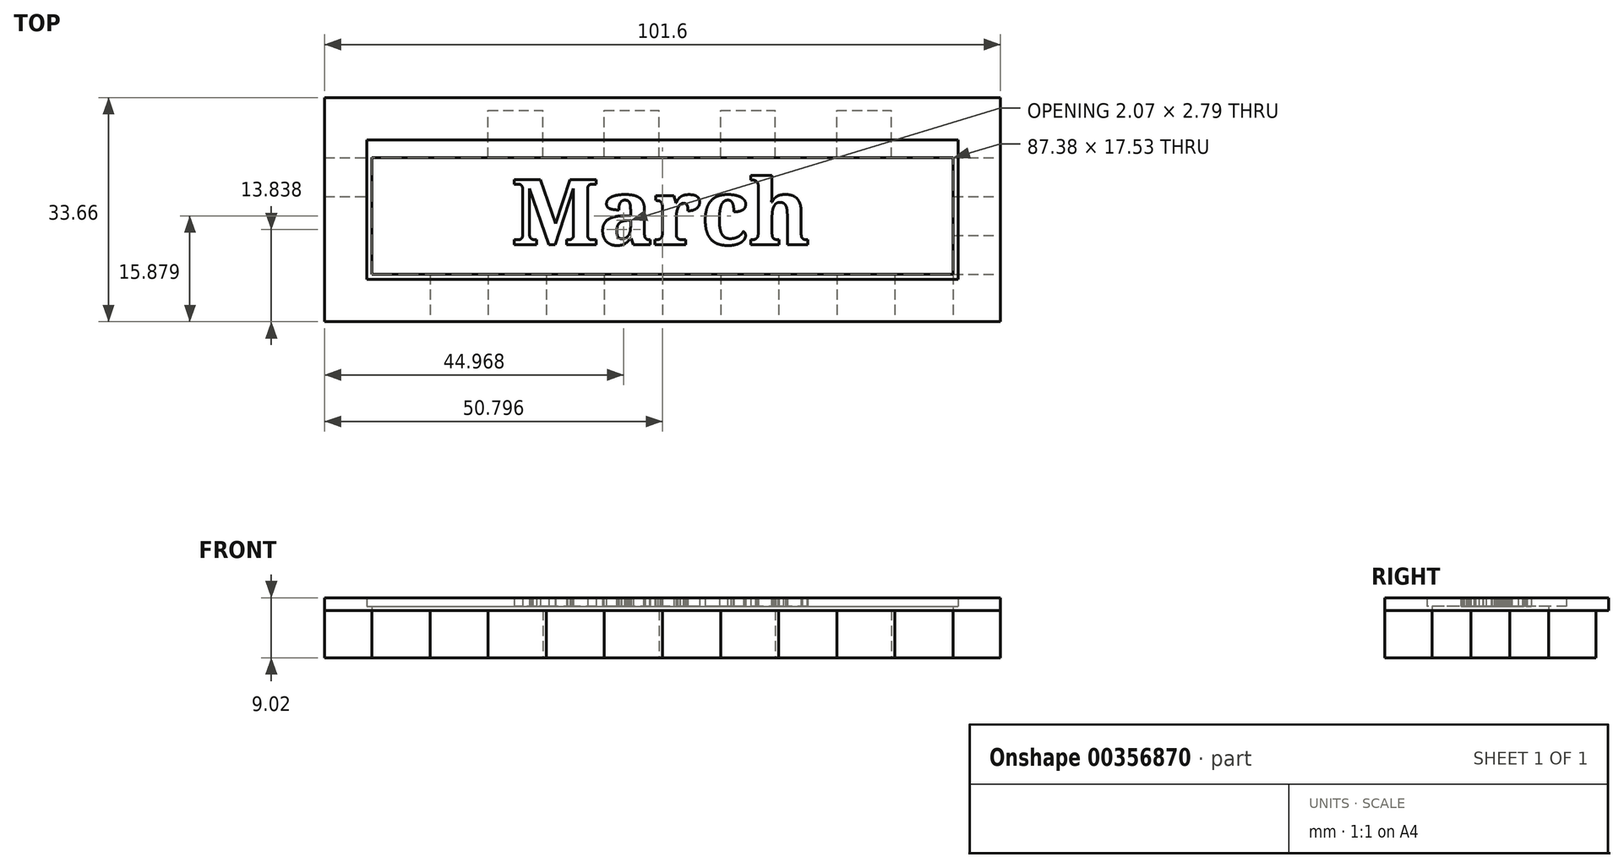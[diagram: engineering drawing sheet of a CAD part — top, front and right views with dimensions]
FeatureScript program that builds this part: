
annotation { "Feature Type Name" : "Feature", "Feature Type Description" : "" }
export const myFeature = defineFeature(function(context is Context, id is Id, definition is map)
    precondition{}
    {
        {
            var Q0;
            Q0=qCreatedBy(makeId("Top.planeOp"),FACE);
            var sketch = newSketch(context, id + "F0", { "sketchPlane" : qUnion([Q0])});
            skLineSegment(sketch, "E0.bottom", {"start": v(-52.12, 11.37) * mm, "end": v(49.48, 11.37) * mm});
            skLineSegment(sketch, "E0.top", {"start": v(-52.12, -20.38) * mm, "end": v(49.48, -20.38) * mm});
            skLineSegment(sketch, "E0.left", {"start": v(-52.12, 11.37) * mm, "end": v(-52.12, -20.38) * mm});
            skLineSegment(sketch, "E0.right", {"start": v(49.48, 11.37) * mm, "end": v(49.48, -20.38) * mm});
            skLineSegment(sketch, "E1.bottom", {"start": v(-52.12, 11.37) * mm, "end": v(-45.01, 11.37) * mm});
            skLineSegment(sketch, "E1.top", {"start": v(-52.12, 4.26) * mm, "end": v(-45.01, 4.26) * mm});
            skLineSegment(sketch, "E1.left", {"start": v(-52.12, 11.37) * mm, "end": v(-52.12, 4.26) * mm});
            skLineSegment(sketch, "E1.right", {"start": v(-45.01, 11.37) * mm, "end": v(-45.01, 4.26) * mm});
            skLineSegment(sketch, "E2.bottom", {"start": v(-45.01, 11.37) * mm, "end": v(-36.78, 11.37) * mm});
            skLineSegment(sketch, "E2.top", {"start": v(-45.01, 4.26) * mm, "end": v(-36.78, 4.26) * mm});
            skLineSegment(sketch, "E2.right", {"start": v(-36.78, 11.37) * mm, "end": v(-36.78, 4.26) * mm});
            skLineSegment(sketch, "E3.bottom", {"start": v(-36.78, 4.26) * mm, "end": v(-27.54, 4.26) * mm});
            skLineSegment(sketch, "E3.top", {"start": v(-36.78, 11.37) * mm, "end": v(-27.54, 11.37) * mm});
            skLineSegment(sketch, "E3.left", {"start": v(-36.78, 4.26) * mm, "end": v(-36.78, 11.37) * mm});
            skLineSegment(sketch, "E3.right", {"start": v(-27.54, 4.26) * mm, "end": v(-27.54, 11.37) * mm});
            skLineSegment(sketch, "E4.bottom", {"start": v(-27.54, 4.26) * mm, "end": v(-19.3, 4.26) * mm});
            skLineSegment(sketch, "E4.top", {"start": v(-27.54, 11.37) * mm, "end": v(-19.3, 11.37) * mm});
            skLineSegment(sketch, "E4.right", {"start": v(-19.3, 4.26) * mm, "end": v(-19.3, 11.37) * mm});
            skLineSegment(sketch, "E5.bottom", {"start": v(-19.3, 4.26) * mm, "end": v(-10.06, 4.26) * mm});
            skLineSegment(sketch, "E5.top", {"start": v(-19.3, 11.37) * mm, "end": v(-10.06, 11.37) * mm});
            skLineSegment(sketch, "E5.right", {"start": v(-10.06, 4.26) * mm, "end": v(-10.06, 11.37) * mm});
            skLineSegment(sketch, "E6.bottom", {"start": v(-10.06, 4.26) * mm, "end": v(-10.06, 4.26) * mm});
            skLineSegment(sketch, "E6.top", {"start": v(-10.06, 11.37) * mm, "end": v(-10.06, 11.37) * mm});
            skLineSegment(sketch, "E7.bottom", {"start": v(-10.06, 4.26) * mm, "end": v(-1.83, 4.26) * mm});
            skLineSegment(sketch, "E7.top", {"start": v(-10.06, 11.37) * mm, "end": v(-1.83, 11.37) * mm});
            skLineSegment(sketch, "E7.right", {"start": v(-1.83, 4.26) * mm, "end": v(-1.83, 11.37) * mm});
            skLineSegment(sketch, "E8.bottom", {"start": v(-1.83, 4.26) * mm, "end": v(7.41, 4.26) * mm});
            skLineSegment(sketch, "E8.top", {"start": v(-1.83, 11.37) * mm, "end": v(7.41, 11.37) * mm});
            skLineSegment(sketch, "E8.right", {"start": v(7.41, 4.26) * mm, "end": v(7.41, 11.37) * mm});
            skLineSegment(sketch, "E9.bottom", {"start": v(7.41, 4.26) * mm, "end": v(15.64, 4.26) * mm});
            skLineSegment(sketch, "E9.top", {"start": v(7.41, 11.37) * mm, "end": v(15.64, 11.37) * mm});
            skLineSegment(sketch, "E9.right", {"start": v(15.64, 4.26) * mm, "end": v(15.64, 11.37) * mm});
            skLineSegment(sketch, "E10.bottom", {"start": v(15.64, 4.26) * mm, "end": v(24.89, 4.26) * mm});
            skLineSegment(sketch, "E10.top", {"start": v(15.64, 11.37) * mm, "end": v(24.89, 11.37) * mm});
            skLineSegment(sketch, "E10.right", {"start": v(24.89, 4.26) * mm, "end": v(24.89, 11.37) * mm});
            skLineSegment(sketch, "E11.bottom", {"start": v(24.89, 4.26) * mm, "end": v(24.89, 4.26) * mm});
            skLineSegment(sketch, "E11.top", {"start": v(24.89, 11.37) * mm, "end": v(24.89, 11.37) * mm});
            skLineSegment(sketch, "E12.bottom", {"start": v(24.89, 4.26) * mm, "end": v(33.12, 4.26) * mm});
            skLineSegment(sketch, "E12.top", {"start": v(24.89, 11.37) * mm, "end": v(33.12, 11.37) * mm});
            skLineSegment(sketch, "E12.right", {"start": v(33.12, 4.26) * mm, "end": v(33.12, 11.37) * mm});
            skLineSegment(sketch, "E13.bottom", {"start": v(33.12, 4.26) * mm, "end": v(42.36, 4.26) * mm});
            skLineSegment(sketch, "E13.top", {"start": v(33.12, 11.37) * mm, "end": v(42.36, 11.37) * mm});
            skLineSegment(sketch, "E13.right", {"start": v(42.36, 4.26) * mm, "end": v(42.36, 11.37) * mm});
            skLineSegment(sketch, "E14.bottom", {"start": v(42.36, 4.26) * mm, "end": v(49.48, 4.26) * mm});
            skLineSegment(sketch, "E14.top", {"start": v(42.36, 11.37) * mm, "end": v(49.48, 11.37) * mm});
            skLineSegment(sketch, "E14.right", {"start": v(49.48, 4.26) * mm, "end": v(49.48, 11.37) * mm});
            skLineSegment(sketch, "E15.bottom", {"start": v(-52.12, -20.38) * mm, "end": v(-45.01, -20.38) * mm});
            skLineSegment(sketch, "E15.top", {"start": v(-52.12, -13.26) * mm, "end": v(-45.01, -13.26) * mm});
            skLineSegment(sketch, "E15.left", {"start": v(-52.12, -20.38) * mm, "end": v(-52.12, -13.26) * mm});
            skLineSegment(sketch, "E15.right", {"start": v(-45.01, -20.38) * mm, "end": v(-45.01, -13.26) * mm});
            skLineSegment(sketch, "E16.bottom", {"start": v(-45.01, -13.26) * mm, "end": v(-45.01, -13.26) * mm});
            skLineSegment(sketch, "E16.top", {"start": v(-45.01, -20.38) * mm, "end": v(-45.01, -20.38) * mm});
            skLineSegment(sketch, "E16.left", {"start": v(-45.01, -13.26) * mm, "end": v(-45.01, -20.38) * mm});
            skLineSegment(sketch, "E16.right", {"start": v(-45.01, -13.26) * mm, "end": v(-45.01, -20.38) * mm});
            skLineSegment(sketch, "E17.bottom", {"start": v(-45.01, -13.26) * mm, "end": v(-36.27, -13.26) * mm});
            skLineSegment(sketch, "E17.top", {"start": v(-45.01, -20.38) * mm, "end": v(-36.27, -20.38) * mm});
            skLineSegment(sketch, "E17.right", {"start": v(-36.27, -13.26) * mm, "end": v(-36.27, -20.38) * mm});
            skLineSegment(sketch, "E18.bottom", {"start": v(-36.27, -13.26) * mm, "end": v(-36.27, -13.26) * mm});
            skLineSegment(sketch, "E18.top", {"start": v(-36.27, -20.38) * mm, "end": v(-36.27, -20.38) * mm});
            skLineSegment(sketch, "E19.bottom", {"start": v(-36.27, -13.26) * mm, "end": v(-27.54, -13.26) * mm});
            skLineSegment(sketch, "E19.top", {"start": v(-36.27, -20.38) * mm, "end": v(-27.54, -20.38) * mm});
            skLineSegment(sketch, "E19.right", {"start": v(-27.54, -13.26) * mm, "end": v(-27.54, -20.38) * mm});
            skLineSegment(sketch, "E20.bottom", {"start": v(-27.54, -13.26) * mm, "end": v(-18.8, -13.26) * mm});
            skLineSegment(sketch, "E20.top", {"start": v(-27.54, -20.38) * mm, "end": v(-18.8, -20.38) * mm});
            skLineSegment(sketch, "E20.right", {"start": v(-18.8, -13.26) * mm, "end": v(-18.8, -20.38) * mm});
            skLineSegment(sketch, "E21.bottom", {"start": v(-18.8, -13.26) * mm, "end": v(-10.06, -13.26) * mm});
            skLineSegment(sketch, "E21.top", {"start": v(-18.8, -20.38) * mm, "end": v(-10.06, -20.38) * mm});
            skLineSegment(sketch, "E21.right", {"start": v(-10.06, -13.26) * mm, "end": v(-10.06, -20.38) * mm});
            skLineSegment(sketch, "E22.bottom", {"start": v(-10.06, -13.26) * mm, "end": v(-1.32, -13.26) * mm});
            skLineSegment(sketch, "E22.top", {"start": v(-10.06, -20.38) * mm, "end": v(-1.32, -20.38) * mm});
            skLineSegment(sketch, "E22.right", {"start": v(-1.32, -13.26) * mm, "end": v(-1.32, -20.38) * mm});
            skLineSegment(sketch, "E23.bottom", {"start": v(-1.32, -13.26) * mm, "end": v(7.41, -13.26) * mm});
            skLineSegment(sketch, "E23.top", {"start": v(-1.32, -20.38) * mm, "end": v(7.41, -20.38) * mm});
            skLineSegment(sketch, "E23.right", {"start": v(7.41, -13.26) * mm, "end": v(7.41, -20.38) * mm});
            skLineSegment(sketch, "E24.bottom", {"start": v(7.41, -13.26) * mm, "end": v(16.15, -13.26) * mm});
            skLineSegment(sketch, "E24.top", {"start": v(7.41, -20.38) * mm, "end": v(16.15, -20.38) * mm});
            skLineSegment(sketch, "E24.right", {"start": v(16.15, -13.26) * mm, "end": v(16.15, -20.38) * mm});
            skLineSegment(sketch, "E25.bottom", {"start": v(16.15, -13.26) * mm, "end": v(24.89, -13.26) * mm});
            skLineSegment(sketch, "E25.top", {"start": v(16.15, -20.38) * mm, "end": v(24.89, -20.38) * mm});
            skLineSegment(sketch, "E25.right", {"start": v(24.89, -13.26) * mm, "end": v(24.89, -20.38) * mm});
            skLineSegment(sketch, "E26.bottom", {"start": v(24.89, -13.26) * mm, "end": v(33.63, -13.26) * mm});
            skLineSegment(sketch, "E26.top", {"start": v(24.89, -20.38) * mm, "end": v(33.63, -20.38) * mm});
            skLineSegment(sketch, "E26.right", {"start": v(33.63, -13.26) * mm, "end": v(33.63, -20.38) * mm});
            skLineSegment(sketch, "E27.bottom", {"start": v(33.63, -13.26) * mm, "end": v(42.36, -13.26) * mm});
            skLineSegment(sketch, "E27.top", {"start": v(33.63, -20.38) * mm, "end": v(42.36, -20.38) * mm});
            skLineSegment(sketch, "E27.right", {"start": v(42.36, -13.26) * mm, "end": v(42.36, -20.38) * mm});
            skLineSegment(sketch, "E28.bottom", {"start": v(42.36, -13.26) * mm, "end": v(49.48, -13.26) * mm});
            skLineSegment(sketch, "E28.top", {"start": v(42.36, -20.38) * mm, "end": v(49.48, -20.38) * mm});
            skLineSegment(sketch, "E28.right", {"start": v(49.48, -13.26) * mm, "end": v(49.48, -20.38) * mm});
            skLineSegment(sketch, "E29.top", {"start": v(-52.12, -1.58) * mm, "end": v(-45.01, -1.58) * mm});
            skLineSegment(sketch, "E29.left", {"start": v(-52.12, 4.26) * mm, "end": v(-52.12, -1.58) * mm});
            skLineSegment(sketch, "E29.right", {"start": v(-45.01, 4.26) * mm, "end": v(-45.01, -1.58) * mm});
            skLineSegment(sketch, "E30.top", {"start": v(-52.12, -7.42) * mm, "end": v(-45.01, -7.42) * mm});
            skLineSegment(sketch, "E30.left", {"start": v(-52.12, -1.58) * mm, "end": v(-52.12, -7.42) * mm});
            skLineSegment(sketch, "E30.right", {"start": v(-45.01, -1.58) * mm, "end": v(-45.01, -7.42) * mm});
            skLineSegment(sketch, "E31.bottom", {"start": v(-45.01, -7.42) * mm, "end": v(-52.12, -7.42) * mm});
            skLineSegment(sketch, "E31.top", {"start": v(-45.01, -13.26) * mm, "end": v(-52.12, -13.26) * mm});
            skLineSegment(sketch, "E31.left", {"start": v(-45.01, -7.42) * mm, "end": v(-45.01, -13.26) * mm});
            skLineSegment(sketch, "E31.right", {"start": v(-52.12, -7.42) * mm, "end": v(-52.12, -13.26) * mm});
            skLineSegment(sketch, "E32.top", {"start": v(42.36, -1.58) * mm, "end": v(49.48, -1.58) * mm});
            skLineSegment(sketch, "E32.left", {"start": v(42.36, 4.26) * mm, "end": v(42.36, -1.58) * mm});
            skLineSegment(sketch, "E32.right", {"start": v(49.48, 4.26) * mm, "end": v(49.48, -1.58) * mm});
            skLineSegment(sketch, "E33.top", {"start": v(42.36, -7.42) * mm, "end": v(49.48, -7.42) * mm});
            skLineSegment(sketch, "E33.left", {"start": v(42.36, -1.58) * mm, "end": v(42.36, -7.42) * mm});
            skLineSegment(sketch, "E33.right", {"start": v(49.48, -1.58) * mm, "end": v(49.48, -7.42) * mm});
            skLineSegment(sketch, "E34.left", {"start": v(42.36, -7.42) * mm, "end": v(42.36, -13.26) * mm});
            skLineSegment(sketch, "E34.right", {"start": v(49.48, -7.42) * mm, "end": v(49.48, -13.26) * mm});
            skSolve(sketch);
        }
        {
            var Q0;
            Q0=makeQuery(id+"F0.imprint","IMPRINT",FACE,{"disambiguationData":[TD([[makeQuery(id+"F0.imprint","IMPRINT",EDGE,{"derivedFrom":sQuery(id+"F0.wireOp",EDGE,"E2.top")}),-1.0]])]});
            var Q1;
            Q1=makeQuery(id+"F0.imprint","IMPRINT",FACE,{"disambiguationData":[TD([[makeQuery(id+"F0.imprint","IMPRINT",EDGE,{"derivedFrom":sQuery(id+"F0.wireOp",EDGE,"E2.bottom")}),-1.0]])]});
            var Q2;
            Q2=makeQuery(id+"F0.imprint","IMPRINT",FACE,{"disambiguationData":[TD([[makeQuery(id+"F0.imprint","IMPRINT",EDGE,{"derivedFrom":sQuery(id+"F0.wireOp",EDGE,"E4.bottom")}),1.0]])]});
            var Q3;
            Q3=makeQuery(id+"F0.imprint","IMPRINT",FACE,{"disambiguationData":[TD([[makeQuery(id+"F0.imprint","IMPRINT",EDGE,{"derivedFrom":sQuery(id+"F0.wireOp",EDGE,"E7.bottom")}),1.0]])]});
            var Q4;
            Q4=makeQuery(id+"F0.imprint","IMPRINT",FACE,{"disambiguationData":[TD([[makeQuery(id+"F0.imprint","IMPRINT",EDGE,{"derivedFrom":sQuery(id+"F0.wireOp",EDGE,"E9.bottom")}),1.0]])]});
            var Q5;
            Q5=makeQuery(id+"F0.imprint","IMPRINT",FACE,{"disambiguationData":[TD([[makeQuery(id+"F0.imprint","IMPRINT",EDGE,{"derivedFrom":sQuery(id+"F0.wireOp",EDGE,"E12.bottom")}),1.0]])]});
            var Q6;
            Q6=makeQuery(id+"F0.imprint","IMPRINT",FACE,{"disambiguationData":[TD([[makeQuery(id+"F0.imprint","IMPRINT",EDGE,{"derivedFrom":sQuery(id+"F0.wireOp",EDGE,"E14.bottom")}),-1.0]])]});
            var Q7;
            Q7=makeQuery(id+"F0.imprint","IMPRINT",FACE,{"disambiguationData":[TD([[makeQuery(id+"F0.imprint","IMPRINT",EDGE,{"derivedFrom":sQuery(id+"F0.wireOp",EDGE,"E33.top")}),-1.0]])]});
            var Q8;
            Q8=makeQuery(id+"F0.imprint","IMPRINT",FACE,{"disambiguationData":[TD([[makeQuery(id+"F0.imprint","IMPRINT",EDGE,{"derivedFrom":sQuery(id+"F0.wireOp",EDGE,"E27.bottom")}),-1.0]])]});
            var Q9;
            Q9=makeQuery(id+"F0.imprint","IMPRINT",FACE,{"disambiguationData":[TD([[makeQuery(id+"F0.imprint","IMPRINT",EDGE,{"derivedFrom":sQuery(id+"F0.wireOp",EDGE,"E25.bottom")}),-1.0]])]});
            var Q10;
            Q10=makeQuery(id+"F0.imprint","IMPRINT",FACE,{"disambiguationData":[TD([[makeQuery(id+"F0.imprint","IMPRINT",EDGE,{"derivedFrom":sQuery(id+"F0.wireOp",EDGE,"E23.bottom")}),-1.0]])]});
            var Q11;
            Q11=makeQuery(id+"F0.imprint","IMPRINT",FACE,{"disambiguationData":[TD([[makeQuery(id+"F0.imprint","IMPRINT",EDGE,{"derivedFrom":sQuery(id+"F0.wireOp",EDGE,"E21.bottom")}),-1.0]])]});
            var Q12;
            Q12=makeQuery(id+"F0.imprint","IMPRINT",FACE,{"disambiguationData":[TD([[makeQuery(id+"F0.imprint","IMPRINT",EDGE,{"derivedFrom":sQuery(id+"F0.wireOp",EDGE,"E19.bottom")}),-1.0]])]});
            var Q13;
            Q13=makeQuery(id+"F0.imprint","IMPRINT",FACE,{"disambiguationData":[TD([[makeQuery(id+"F0.imprint","IMPRINT",EDGE,{"derivedFrom":sQuery(id+"F0.wireOp",EDGE,"E31.bottom")}),1.0]])]});
            var Q14;
            Q14=makeQuery(id+"F0.imprint","IMPRINT",FACE,{"disambiguationData":[TD([[makeQuery(id+"F0.imprint","IMPRINT",EDGE,{"derivedFrom":sQuery(id+"F0.wireOp",EDGE,"E1.top")}),-1.0]])]});
            extrude(context, id + "F1", {"entities" : qUnion([Q0, Q1, Q2, Q3, Q4, Q5, Q6, Q7, Q8, Q9, Q10, Q11, Q12, Q13, Q14]), "depth" : 7.11 * mm});
        }
        {
            var Q0;
            Q0=makeQuery(id+"F1.opExtrude","CAP_FACE",FACE,{"disambiguationData":[OSD([sQuery(id+"F0.wireOp",EDGE,"E2.bottom"),sQuery(id+"F0.wireOp",EDGE,"E1.right"),sQuery(id+"F0.wireOp",EDGE,"E3.bottom"),sQuery(id+"F0.wireOp",EDGE,"E3.left"),sQuery(id+"F0.wireOp",EDGE,"E4.top"),sQuery(id+"F0.wireOp",EDGE,"E3.right"),sQuery(id+"F0.wireOp",EDGE,"E5.bottom"),sQuery(id+"F0.wireOp",EDGE,"E4.right"),sQuery(id+"F0.wireOp",EDGE,"E6.top"),sQuery(id+"F0.wireOp",EDGE,"E5.right"),sQuery(id+"F0.wireOp",EDGE,"E7.bottom"),sQuery(id+"F0.wireOp",EDGE,"E5.right"),sQuery(id+"F0.wireOp",EDGE,"E8.top"),sQuery(id+"F0.wireOp",EDGE,"E7.right"),sQuery(id+"F0.wireOp",EDGE,"E9.bottom"),sQuery(id+"F0.wireOp",EDGE,"E8.right"),sQuery(id+"F0.wireOp",EDGE,"E10.top"),sQuery(id+"F0.wireOp",EDGE,"E9.right"),sQuery(id+"F0.wireOp",EDGE,"E11.bottom"),sQuery(id+"F0.wireOp",EDGE,"E10.right"),sQuery(id+"F0.wireOp",EDGE,"E12.top"),sQuery(id+"F0.wireOp",EDGE,"E10.right"),sQuery(id+"F0.wireOp",EDGE,"E13.bottom"),sQuery(id+"F0.wireOp",EDGE,"E12.right"),sQuery(id+"F0.wireOp",EDGE,"E16.bottom"),sQuery(id+"F0.wireOp",EDGE,"E17.top"),sQuery(id+"F0.wireOp",EDGE,"E16.left"),sQuery(id+"F0.wireOp",EDGE,"E18.bottom"),sQuery(id+"F0.wireOp",EDGE,"E17.right"),sQuery(id+"F0.wireOp",EDGE,"E19.top"),sQuery(id+"F0.wireOp",EDGE,"E17.right"),sQuery(id+"F0.wireOp",EDGE,"E20.bottom"),sQuery(id+"F0.wireOp",EDGE,"E19.right"),sQuery(id+"F0.wireOp",EDGE,"E21.top"),sQuery(id+"F0.wireOp",EDGE,"E20.right"),sQuery(id+"F0.wireOp",EDGE,"E22.bottom"),sQuery(id+"F0.wireOp",EDGE,"E21.right"),sQuery(id+"F0.wireOp",EDGE,"E23.top"),sQuery(id+"F0.wireOp",EDGE,"E22.right"),sQuery(id+"F0.wireOp",EDGE,"E24.bottom"),sQuery(id+"F0.wireOp",EDGE,"E23.right"),sQuery(id+"F0.wireOp",EDGE,"E25.top"),sQuery(id+"F0.wireOp",EDGE,"E24.right"),sQuery(id+"F0.wireOp",EDGE,"E26.bottom"),sQuery(id+"F0.wireOp",EDGE,"E25.right"),sQuery(id+"F0.wireOp",EDGE,"E27.top"),sQuery(id+"F0.wireOp",EDGE,"E26.right"),sQuery(id+"F0.wireOp",EDGE,"E27.right"),sQuery(id+"F0.wireOp",EDGE,"E1.top"),sQuery(id+"F0.wireOp",EDGE,"E29.left"),sQuery(id+"F0.wireOp",EDGE,"E29.top"),sQuery(id+"F0.wireOp",EDGE,"E30.right"),sQuery(id+"F0.wireOp",EDGE,"E31.bottom"),sQuery(id+"F0.wireOp",EDGE,"E31.top"),sQuery(id+"F0.wireOp",EDGE,"E31.right"),sQuery(id+"F0.wireOp",EDGE,"E14.bottom"),sQuery(id+"F0.wireOp",EDGE,"E32.right"),sQuery(id+"F0.wireOp",EDGE,"E32.top"),sQuery(id+"F0.wireOp",EDGE,"E33.left"),sQuery(id+"F0.wireOp",EDGE,"E33.top"),sQuery(id+"F0.wireOp",EDGE,"E28.bottom"),sQuery(id+"F0.wireOp",EDGE,"E34.right")])],"isStart":false});
            var sketch = newSketch(context, id + "F2", { "sketchPlane" : qUnion([Q0])});
            skLineSegment(sketch, "E35.bottom", {"start": v(-52.12, -20.38) * mm, "end": v(-45.01, -20.38) * mm});
            skLineSegment(sketch, "E35.top", {"start": v(-52.12, 13.28) * mm, "end": v(-45.01, 13.28) * mm});
            skLineSegment(sketch, "E35.left", {"start": v(-52.12, -20.38) * mm, "end": v(-52.12, 13.28) * mm});
            skLineSegment(sketch, "E35.right", {"start": v(-45.01, -20.38) * mm, "end": v(-45.01, 13.28) * mm});
            skLineSegment(sketch, "E36.bottom", {"start": v(-52.12, -20.38) * mm, "end": v(49.48, -20.38) * mm});
            skLineSegment(sketch, "E36.top", {"start": v(-52.12, -13.26) * mm, "end": v(49.48, -13.26) * mm});
            skLineSegment(sketch, "E36.left", {"start": v(-52.12, -20.38) * mm, "end": v(-52.12, -13.26) * mm});
            skLineSegment(sketch, "E36.right", {"start": v(49.48, -20.38) * mm, "end": v(49.48, -13.26) * mm});
            skPoint(sketch, "E37.oppositeSnap0", {"position": v(42.36, -4.5) * mm});
            skLineSegment(sketch, "E37.bottom", {"start": v(49.48, -20.38) * mm, "end": v(42.36, -20.38) * mm});
            skLineSegment(sketch, "E37.top", {"start": v(49.48, 13.28) * mm, "end": v(42.36, 13.28) * mm});
            skLineSegment(sketch, "E37.left", {"start": v(49.48, -20.38) * mm, "end": v(49.48, 13.28) * mm});
            skLineSegment(sketch, "E37.right", {"start": v(42.36, -20.38) * mm, "end": v(42.36, 13.28) * mm});
            skLineSegment(sketch, "E38.bottom", {"start": v(-52.12, 13.28) * mm, "end": v(49.48, 13.28) * mm});
            skLineSegment(sketch, "E38.top", {"start": v(-52.12, 4.26) * mm, "end": v(49.48, 4.26) * mm});
            skLineSegment(sketch, "E38.left", {"start": v(-52.12, 13.28) * mm, "end": v(-52.12, 4.26) * mm});
            skLineSegment(sketch, "E38.right", {"start": v(49.48, 13.28) * mm, "end": v(49.48, 4.26) * mm});
            skSolve(sketch);
        }
        {
            var Q0;
            Q0=qSketchRegion(id+"F2",true);
            var Q1;
            {var subQ5=sQuery(id+"F2.wireOp",EDGE,"E36.top");var subQ10=sQuery(id+"F2.wireOp",EDGE,"E35.right");var subQ12=makeQuery(id+"F2.imprint","INTERSECT",VERTEX,{"derivedFrom":[makeQuery(id+"F1.opExtrude","CAP_EDGE",EDGE,{"disambiguationData":[OSD([sQuery(id+"F0.wireOp",EDGE,"E31.bottom")])],"isStart":false}),subQ10]});var subQ24=makeQuery(id+"F2.imprint","INTERSECT",VERTEX,{"derivedFrom":[subQ10,subQ5]});Q1=makeQuery(id+"F2.imprint","IMPRINT",FACE,{"disambiguationData":[TD([[makeQuery(id+"F2.imprint","IMPRINT",EDGE,{"disambiguationData":[TD([[subQ12,1.0],[subQ24,-1.0]])],"derivedFrom":subQ10}),-1.0]])]});}
            extrude(context, id + "F3", {"entities" : qUnion([Q0, Q1]), "depth" : 0.64 * mm});
        }
        {
            var Q0;
            Q0=makeQuery(id+"F3.opExtrude","CAP_FACE",FACE,{"disambiguationData":[OSD([sQuery(id+"F2.wireOp",EDGE,"E35.left"),sQuery(id+"F2.wireOp",EDGE,"E36.bottom"),sQuery(id+"F2.wireOp",EDGE,"E36.left"),sQuery(id+"F2.wireOp",EDGE,"E37.bottom"),sQuery(id+"F2.wireOp",EDGE,"E37.left"),sQuery(id+"F2.wireOp",EDGE,"E38.bottom"),sQuery(id+"F2.wireOp",EDGE,"E38.left"),sQuery(id+"F2.wireOp",EDGE,"E38.right")])],"isStart":false});
            var sketch = newSketch(context, id + "F4", { "sketchPlane" : qUnion([Q0])});
            skLineSegment(sketch, "E39.bottom", {"start": v(-52.12, 13.28) * mm, "end": v(49.48, 13.28) * mm});
            skLineSegment(sketch, "E39.top", {"start": v(-52.12, 6.93) * mm, "end": v(49.48, 6.93) * mm});
            skLineSegment(sketch, "E39.left", {"start": v(-52.12, 13.28) * mm, "end": v(-52.12, 6.93) * mm});
            skLineSegment(sketch, "E39.right", {"start": v(49.48, 13.28) * mm, "end": v(49.48, 6.93) * mm});
            skLineSegment(sketch, "E40.bottom", {"start": v(-52.12, 13.28) * mm, "end": v(-45.77, 13.28) * mm});
            skLineSegment(sketch, "E40.top", {"start": v(-52.12, -20.38) * mm, "end": v(-45.77, -20.38) * mm});
            skLineSegment(sketch, "E40.left", {"start": v(-52.12, 13.28) * mm, "end": v(-52.12, -20.38) * mm});
            skLineSegment(sketch, "E40.right", {"start": v(-45.77, 13.28) * mm, "end": v(-45.77, -20.38) * mm});
            skLineSegment(sketch, "E41.bottom", {"start": v(-52.12, -14.03) * mm, "end": v(49.48, -14.03) * mm});
            skLineSegment(sketch, "E41.top", {"start": v(-52.12, -20.38) * mm, "end": v(49.48, -20.38) * mm});
            skLineSegment(sketch, "E41.left", {"start": v(-52.12, -14.03) * mm, "end": v(-52.12, -20.38) * mm});
            skLineSegment(sketch, "E41.right", {"start": v(49.48, -14.03) * mm, "end": v(49.48, -20.38) * mm});
            skLineSegment(sketch, "E42.bottom", {"start": v(49.48, -20.38) * mm, "end": v(43.13, -20.38) * mm});
            skLineSegment(sketch, "E42.top", {"start": v(49.48, 13.28) * mm, "end": v(43.13, 13.28) * mm});
            skLineSegment(sketch, "E42.left", {"start": v(49.48, -20.38) * mm, "end": v(49.48, 13.28) * mm});
            skLineSegment(sketch, "E42.right", {"start": v(43.13, -20.38) * mm, "end": v(43.13, 13.28) * mm});
            skSolve(sketch);
        }
        {
            var Q0;
            Q0=qSketchRegion(id+"F4",true);
            extrude(context, id + "F5", {"entities" : qUnion([Q0]), "operationType" : NewBodyOperationType.ADD, "depth" : 1.27 * mm});
        }
        {
            var Q0;
            Q0=makeQuery(id+"F3.opExtrude","CAP_FACE",FACE,{"disambiguationData":[OSD([sQuery(id+"F2.wireOp",EDGE,"E35.left"),sQuery(id+"F2.wireOp",EDGE,"E36.bottom"),sQuery(id+"F2.wireOp",EDGE,"E36.left"),sQuery(id+"F2.wireOp",EDGE,"E37.bottom"),sQuery(id+"F2.wireOp",EDGE,"E37.left"),sQuery(id+"F2.wireOp",EDGE,"E38.bottom"),sQuery(id+"F2.wireOp",EDGE,"E38.left"),sQuery(id+"F2.wireOp",EDGE,"E38.right")])],"isStart":false});
            var sketch = newSketch(context, id + "F6", { "sketchPlane" : qUnion([Q0])});
            skText(sketch, "E43", { "text": "March", "fontName": "NotoSerif-Bold.ttf"});
            const initialGuessF6  = {"E43": [-0.024, -0.0088, 1, 0, 0.00988]};
            skSetInitialGuess(sketch, initialGuessF6);
            skSolve(sketch);
        }
        {
            var Q0;
            Q0 = qSketchRegion(id + "F6", true);
            extrude(context, id + "F7", {"entities" : qUnion([Q0]), "operationType" : NewBodyOperationType.ADD, "depth" : 1.27 * mm});
        }
    });
